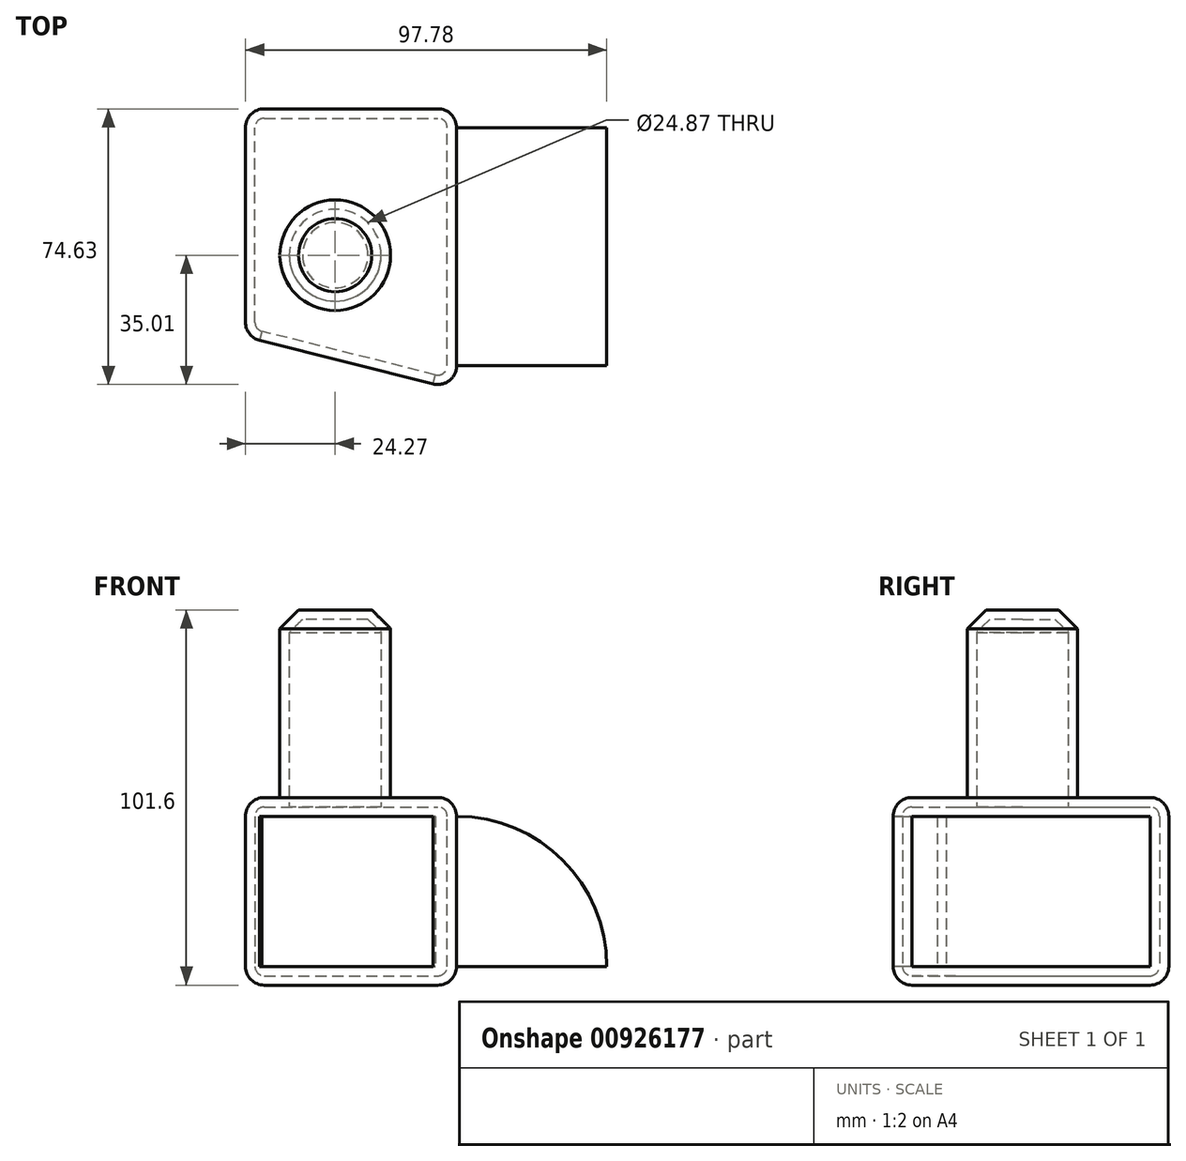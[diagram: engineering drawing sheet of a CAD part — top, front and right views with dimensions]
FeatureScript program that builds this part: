
annotation { "Feature Type Name" : "Feature", "Feature Type Description" : "" }
export const myFeature = defineFeature(function(context is Context, id is Id, definition is map)
    precondition{}
    {
        {
            var Q0;
            Q0=qCreatedBy(makeId("Top.planeOp"),FACE);
            var sketch = newSketch(context, id + "F0", { "sketchPlane" : qUnion([Q0])});
            skLineSegment(sketch, "E0", {"start": v(32.87, -36.44) * mm, "end": v(32.87, 39.62) * mm});
            skLineSegment(sketch, "E1", {"start": v(32.87, 39.62) * mm, "end": v(-24.27, 39.62) * mm});
            skLineSegment(sketch, "E2", {"start": v(-24.27, 39.62) * mm, "end": v(-24.27, -22.11) * mm});
            skLineSegment(sketch, "E3", {"start": v(-24.27, -22.11) * mm, "end": v(32.87, -36.44) * mm});
            skSolve(sketch);
        }
        {
            var Q0;
            Q0 = qSketchRegion(id + "F0", true);
            extrude(context, id + "F1", {"entities" : qUnion([Q0]), "depth" : 50.8 * mm, "offsetDistance" : 25.4 * mm});
        }
        {
            var Q0;
            Q0=makeQuery(id+"F1.opExtrude","SWEPT_EDGE",EDGE,{"disambiguationData":[OSD([sQuery(id+"F0.wireOp",EDGE,"E0"),sQuery(id+"F0.wireOp",EDGE,"E3")])]});
            var Q1;
            Q1=makeQuery(id+"F1.opExtrude","SWEPT_EDGE",EDGE,{"disambiguationData":[OSD([sQuery(id+"F0.wireOp",EDGE,"E1"),sQuery(id+"F0.wireOp",EDGE,"E2")])]});
            var Q2;
            Q2=makeQuery(id+"F1.opExtrude","CAP_EDGE",EDGE,{"disambiguationData":[OSD([sQuery(id+"F0.wireOp",EDGE,"E0")])],"isStart":true});
            var Q3;
            Q3=makeQuery(id+"F1.opExtrude","CAP_EDGE",EDGE,{"disambiguationData":[OSD([sQuery(id+"F0.wireOp",EDGE,"E0")])],"isStart":false});
            var Q4;
            Q4=makeQuery(id+"F1.opExtrude","CAP_EDGE",EDGE,{"disambiguationData":[OSD([sQuery(id+"F0.wireOp",EDGE,"E2")])],"isStart":false});
            var Q5;
            Q5=makeQuery(id+"F1.opExtrude","CAP_EDGE",EDGE,{"disambiguationData":[OSD([sQuery(id+"F0.wireOp",EDGE,"E3")])],"isStart":false});
            var Q6;
            Q6=makeQuery(id+"F1.opExtrude","SWEPT_EDGE",EDGE,{"disambiguationData":[OSD([sQuery(id+"F0.wireOp",EDGE,"E0"),sQuery(id+"F0.wireOp",EDGE,"E1")])]});
            var Q7;
            Q7=makeQuery(id+"F1.opExtrude","SWEPT_EDGE",EDGE,{"disambiguationData":[OSD([sQuery(id+"F0.wireOp",EDGE,"E2"),sQuery(id+"F0.wireOp",EDGE,"E3")])]});
            var Q8;
            Q8=makeQuery(id+"F1.opExtrude","CAP_EDGE",EDGE,{"disambiguationData":[OSD([sQuery(id+"F0.wireOp",EDGE,"E1")])],"isStart":true});
            var Q9;
            Q9=makeQuery(id+"F1.opExtrude","CAP_EDGE",EDGE,{"disambiguationData":[OSD([sQuery(id+"F0.wireOp",EDGE,"E1")])],"isStart":false});
            var Q10;
            Q10=makeQuery(id+"F1.opExtrude","CAP_EDGE",EDGE,{"disambiguationData":[OSD([sQuery(id+"F0.wireOp",EDGE,"E2")])],"isStart":true});
            var Q11;
            Q11=makeQuery(id+"F1.opExtrude","CAP_EDGE",EDGE,{"disambiguationData":[OSD([sQuery(id+"F0.wireOp",EDGE,"E3")])],"isStart":true});
            fillet(context, id + "F2", {"entities" : qUnion([Q0, Q1, Q2, Q3, Q4, Q5, Q6, Q7, Q8, Q9, Q10, Q11]), "radius" : 5.08 * mm, "tangentPropagation" : true, "allowEdgeOverflow" : false});
        }
        {
            var Q0;
            Q0=makeQuery(id+"F1.opExtrude","CAP_FACE",FACE,{"disambiguationData":[OSD([sQuery(id+"F0.wireOp",EDGE,"E0"),sQuery(id+"F0.wireOp",EDGE,"E1"),sQuery(id+"F0.wireOp",EDGE,"E2"),sQuery(id+"F0.wireOp",EDGE,"E3")])],"isStart":false});
            var sketch = newSketch(context, id + "F3", { "sketchPlane" : qUnion([Q0])});
            skCircle(sketch, "E4", {"center": v(0, 0) * mm, "radius": 14.97 * mm});
            skSolve(sketch);
        }
        {
            var Q0;
            Q0 = qSketchRegion(id + "F3", true);
            extrude(context, id + "F4", {"entities" : qUnion([Q0]), "operationType" : NewBodyOperationType.ADD, "depth" : 50.8 * mm, "offsetDistance" : 25.4 * mm});
        }
        {
            var Q0;
            Q0=makeQuery(id+"F4.opExtrude","CAP_EDGE",EDGE,{"disambiguationData":[OSD([sQuery(id+"F3.wireOp",EDGE,"E4")])],"isStart":false});
            chamfer(context, id + "F5", {"entities" : qUnion([Q0]), "width" : 5.08 * mm, "tangentPropagation" : true});
        }
        {
            var Q0;
            Q0=makeQuery(id+"F1.opExtrude","SWEPT_FACE",FACE,{"disambiguationData":[OSD([sQuery(id+"F0.wireOp",EDGE,"E3")])]});
            shell(context, id + "F6", {"entities" : qUnion([Q0]), "thickness" : 2.54 * mm});
        }
        {
            var Q0;
            Q0=makeQuery(id+"F1.opExtrude","SWEPT_FACE",FACE,{"disambiguationData":[OSD([sQuery(id+"F0.wireOp",EDGE,"E0")])]});
            var Q1;
            {var subQ0=sQuery(id+"F0.wireOp",EDGE,"E0");Q1=makeQuery(id+"F2.opFillet","BLEND_EDGE",EDGE,{"blendedFrom":[makeQuery(id+"F1.opExtrude","CAP_EDGE",EDGE,{"disambiguationData":[OSD([subQ0])],"isStart":true}),makeQuery(id+"F1.opExtrude","SWEPT_FACE",FACE,{"disambiguationData":[OSD([subQ0])]})],"blendedInto":[makeQuery(id+"F1.opExtrude","SWEPT_FACE",FACE,{"disambiguationData":[OSD([subQ0])]})]});}
            revolve(context, id + "F7", {"operationType" : NewBodyOperationType.ADD, "surfaceOperationType" : NewSurfaceOperationType.NEW, "entities" : qUnion([Q0]), "axis" : qUnion([Q1]), "revolveType" : RevolveType.ONE_DIRECTION, "angle" : 90 * degree});
        }
    });
